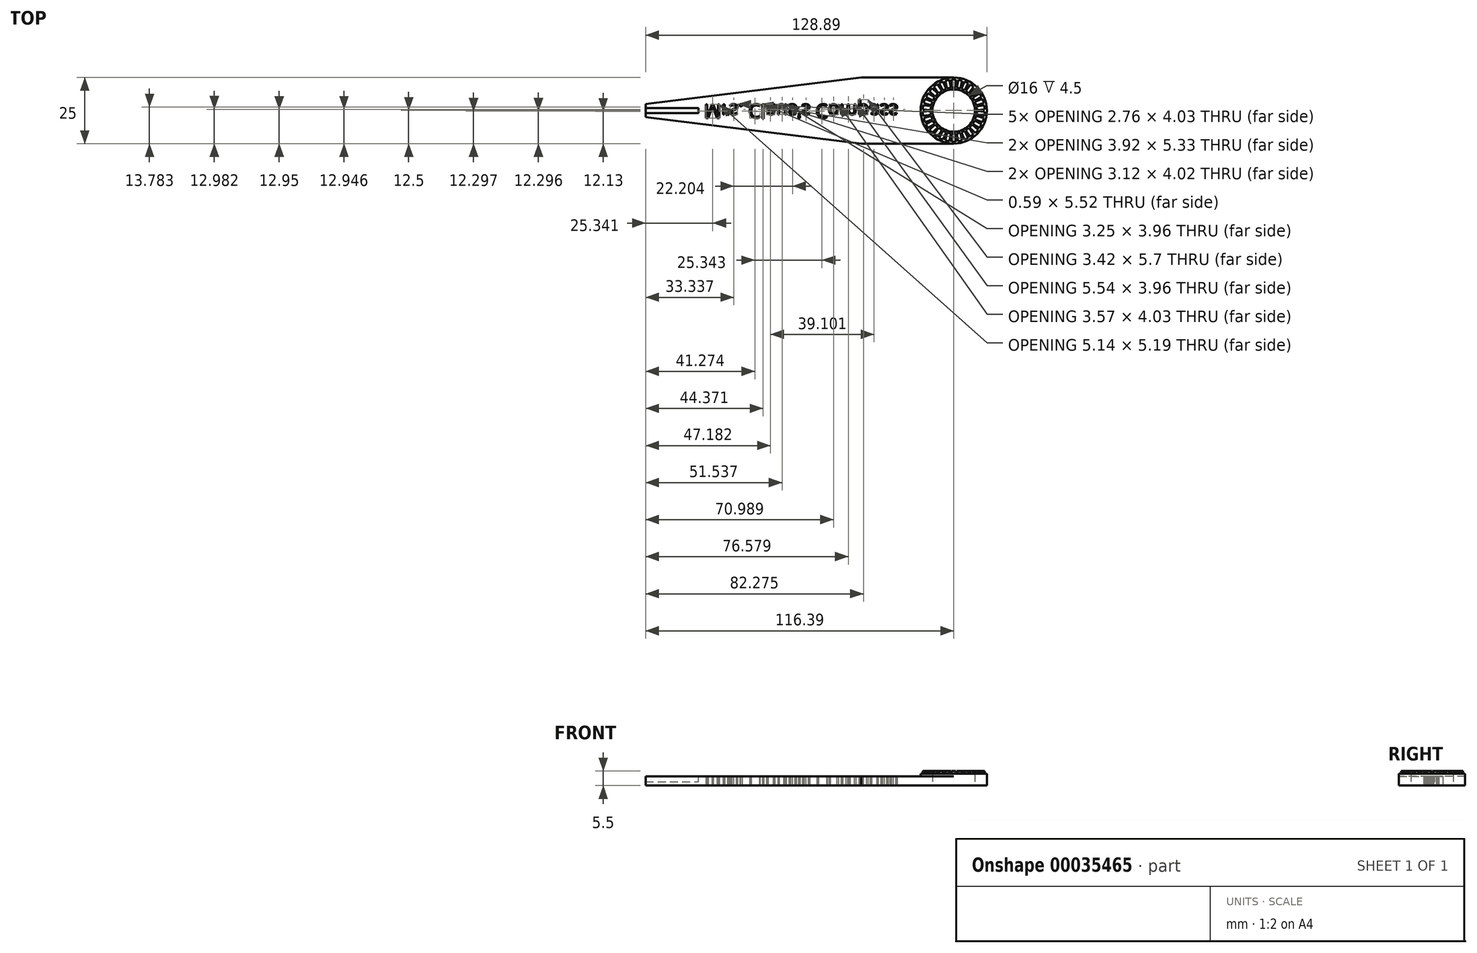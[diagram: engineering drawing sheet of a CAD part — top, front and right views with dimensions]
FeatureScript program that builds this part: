
annotation { "Feature Type Name" : "Feature", "Feature Type Description" : "" }
export const myFeature = defineFeature(function(context is Context, id is Id, definition is map)
    precondition{}
    {
        {
            var Q0;
            Q0=qCreatedBy(makeId("Top.planeOp"),FACE);
            var sketch = newSketch(context, id + "F0", { "sketchPlane" : qUnion([Q0])});
            skCircle(sketch, "E0", {"center": v(0, 0) * mm, "radius": 8 * mm});
            skCircle(sketch, "E1", {"center": v(0, 0) * mm, "radius": 12.5 * mm});
            skLineSegment(sketch, "E2", {"start": v(-35, 12.5) * mm, "end": v(0, 12.5) * mm});
            skLineSegment(sketch, "E3", {"start": v(-35, -12.5) * mm, "end": v(0, -12.5) * mm});
            skLineSegment(sketch, "E4", {"start": v(-35, 12.5) * mm, "end": v(-121.89, 12.5) * mm, "construction": true});
            skLineSegment(sketch, "E5", {"start": v(-35, 12.5) * mm, "end": v(-116.39, 2.5) * mm});
            skLineSegment(sketch, "E6", {"start": v(-35, -12.5) * mm, "end": v(-123.5, -12.5) * mm, "construction": true});
            skLineSegment(sketch, "E7", {"start": v(-35, -12.5) * mm, "end": v(-116.39, -2.5) * mm});
            skLineSegment(sketch, "E8", {"start": v(-116.39, 2.5) * mm, "end": v(-116.39, -2.5) * mm});
            skSolve(sketch);
        }
        {
            var Q0;
            Q0 = qSketchRegion(id + "F0", true);
            var Q1;
            Q1 = qSketchRegion(id + "F3", true);
            extrude(context, id + "F1", {"entities" : qUnion([Q0, Q1]), "depth" : 3.5 * mm});
        }
        {
            var Q0;
            Q0=makeQuery(id+"F1.opExtrude","CAP_FACE",FACE,{"disambiguationData":[OSD([sQuery(id+"F0.wireOp",EDGE,"E0"),sQuery(id+"F0.wireOp",EDGE,"E1"),sQuery(id+"F0.wireOp",EDGE,"E2"),sQuery(id+"F0.wireOp",EDGE,"E3"),sQuery(id+"F0.wireOp",EDGE,"E5"),sQuery(id+"F0.wireOp",EDGE,"E7"),sQuery(id+"F0.wireOp",EDGE,"E8")])],"isStart":false});
            var sketch = newSketch(context, id + "F2", { "sketchPlane" : qUnion([Q0])});
            skCircle(sketch, "E9", {"center": v(0, 0) * mm, "radius": 12.5 * mm});
            skCircle(sketch, "E10", {"center": v(0, 0) * mm, "radius": 8 * mm});
            skSolve(sketch);
        }
        {
            var Q0;
            {var subQ1=makeQuery(id+"F1.opExtrude","CAP_EDGE",EDGE,{"disambiguationData":[OSD([sQuery(id+"F0.wireOp",EDGE,"E2")])],"isStart":false});Q0=makeQuery(id+"F2.imprint","IMPRINT",FACE,{"disambiguationData":[TD([[makeQuery(id+"F2.imprint","IMPRINT",EDGE,{"derivedFrom":subQ1}),-1.0]])]});}
            var sketch = newSketch(context, id + "F3", { "sketchPlane" : qUnion([Q0])});
            skSolve(sketch);
        }
        {
            var Q0;
            {var subQ1=makeQuery(id+"F1.opExtrude","CAP_EDGE",EDGE,{"disambiguationData":[OSD([sQuery(id+"F0.wireOp",EDGE,"E2")])],"isStart":false});Q0=makeQuery(id+"F2.imprint","IMPRINT",FACE,{"disambiguationData":[TD([[makeQuery(id+"F2.imprint","IMPRINT",EDGE,{"derivedFrom":subQ1}),-1.0]])]});}
            var sketch = newSketch(context, id + "F4", { "sketchPlane" : qUnion([Q0])});
            skLineSegment(sketch, "E11.bottom", {"start": v(-116.39, 1) * mm, "end": v(-96.39, 1) * mm});
            skLineSegment(sketch, "E11.top", {"start": v(-116.39, -1) * mm, "end": v(-96.39, -1) * mm});
            skLineSegment(sketch, "E11.left", {"start": v(-116.39, 1) * mm, "end": v(-116.39, -1) * mm});
            skLineSegment(sketch, "E11.right", {"start": v(-96.39, 1) * mm, "end": v(-96.39, -1) * mm});
            skSolve(sketch);
        }
        {
            var Q0;
            Q0 = qSketchRegion(id + "F4", true);
            extrude(context, id + "F5", {"entities" : qUnion([Q0]), "operationType" : NewBodyOperationType.REMOVE, "oppositeDirection" : true, "depth" : 2 * mm});
        }
        {
            var Q0;
            Q0 = qSketchRegion(id + "F2", true);
            extrude(context, id + "F6", {"entities" : qUnion([Q0]), "operationType" : NewBodyOperationType.ADD, "depth" : 1 * mm});
        }
        {
            var Q0;
            Q0=makeQuery(id+"F6.opExtrude","CAP_FACE",FACE,{"disambiguationData":[OSD([sQuery(id+"F2.wireOp",EDGE,"E9"),sQuery(id+"F2.wireOp",EDGE,"E10")])],"isStart":false});
            var sketch = newSketch(context, id + "F7", { "sketchPlane" : qUnion([Q0])});
            skLineSegment(sketch, "E12.bottom", {"start": v(-0.74, 11.7) * mm, "end": v(0.76, 11.7) * mm});
            skLineSegment(sketch, "E12.top", {"start": v(-0.74, 8.7) * mm, "end": v(0.76, 8.7) * mm});
            skLineSegment(sketch, "E12.left", {"start": v(-0.74, 11.7) * mm, "end": v(-0.74, 8.7) * mm});
            skLineSegment(sketch, "E12.right", {"start": v(0.76, 11.7) * mm, "end": v(0.76, 8.7) * mm});
            skLineSegment(sketch, "E13.1.0", {"start": v(-3.16, 11.28) * mm, "end": v(-2.53, 8.35) * mm});
            skLineSegment(sketch, "E13.1.1", {"start": v(-2.53, 8.35) * mm, "end": v(-1.07, 8.66) * mm});
            skLineSegment(sketch, "E13.1.2", {"start": v(-1.7, 11.6) * mm, "end": v(-1.07, 8.66) * mm});
            skLineSegment(sketch, "E13.1.3", {"start": v(-3.16, 11.28) * mm, "end": v(-1.7, 11.6) * mm});
            skLineSegment(sketch, "E13.2.0", {"start": v(-5.44, 10.38) * mm, "end": v(-4.21, 7.64) * mm});
            skLineSegment(sketch, "E13.2.1", {"start": v(-4.21, 7.64) * mm, "end": v(-2.84, 8.25) * mm});
            skLineSegment(sketch, "E13.2.2", {"start": v(-4.06, 11) * mm, "end": v(-2.84, 8.25) * mm});
            skLineSegment(sketch, "E13.2.3", {"start": v(-5.44, 10.38) * mm, "end": v(-4.06, 11) * mm});
            skLineSegment(sketch, "E13.3.0", {"start": v(-7.47, 9.02) * mm, "end": v(-5.71, 6.6) * mm});
            skLineSegment(sketch, "E13.3.1", {"start": v(-5.71, 6.6) * mm, "end": v(-4.5, 7.48) * mm});
            skLineSegment(sketch, "E13.3.2", {"start": v(-6.26, 9.9) * mm, "end": v(-4.5, 7.48) * mm});
            skLineSegment(sketch, "E13.3.3", {"start": v(-7.47, 9.02) * mm, "end": v(-6.26, 9.9) * mm});
            skLineSegment(sketch, "E13.4.0", {"start": v(-9.19, 7.27) * mm, "end": v(-6.96, 5.27) * mm});
            skLineSegment(sketch, "E13.4.1", {"start": v(-6.96, 5.27) * mm, "end": v(-5.95, 6.38) * mm});
            skLineSegment(sketch, "E13.4.2", {"start": v(-8.18, 8.39) * mm, "end": v(-5.95, 6.38) * mm});
            skLineSegment(sketch, "E13.4.3", {"start": v(-9.19, 7.27) * mm, "end": v(-8.18, 8.39) * mm});
            skLineSegment(sketch, "E13.5.0", {"start": v(-10.5, 5.2) * mm, "end": v(-7.9, 3.7) * mm});
            skLineSegment(sketch, "E13.5.1", {"start": v(-7.9, 3.7) * mm, "end": v(-7.15, 5) * mm});
            skLineSegment(sketch, "E13.5.2", {"start": v(-9.75, 6.5) * mm, "end": v(-7.15, 5) * mm});
            skLineSegment(sketch, "E13.5.3", {"start": v(-10.5, 5.2) * mm, "end": v(-9.75, 6.5) * mm});
            skLineSegment(sketch, "E13.6.0", {"start": v(-11.35, 2.9) * mm, "end": v(-8.5, 1.98) * mm});
            skLineSegment(sketch, "E13.6.1", {"start": v(-8.5, 1.98) * mm, "end": v(-8.03, 3.4) * mm});
            skLineSegment(sketch, "E13.6.2", {"start": v(-10.89, 4.33) * mm, "end": v(-8.03, 3.4) * mm});
            skLineSegment(sketch, "E13.6.3", {"start": v(-11.35, 2.9) * mm, "end": v(-10.89, 4.33) * mm});
            skLineSegment(sketch, "E13.7.0", {"start": v(-11.7, 0.48) * mm, "end": v(-8.72, 0.17) * mm});
            skLineSegment(sketch, "E13.7.1", {"start": v(-8.72, 0.17) * mm, "end": v(-8.57, 1.66) * mm});
            skLineSegment(sketch, "E13.7.2", {"start": v(-11.55, 1.98) * mm, "end": v(-8.57, 1.66) * mm});
            skLineSegment(sketch, "E13.7.3", {"start": v(-11.7, 0.48) * mm, "end": v(-11.55, 1.98) * mm});
            skLineSegment(sketch, "E13.8.0", {"start": v(-11.55, -1.96) * mm, "end": v(-8.57, -1.65) * mm});
            skLineSegment(sketch, "E13.8.1", {"start": v(-8.57, -1.65) * mm, "end": v(-8.73, -0.16) * mm});
            skLineSegment(sketch, "E13.8.2", {"start": v(-11.7, -0.47) * mm, "end": v(-8.73, -0.16) * mm});
            skLineSegment(sketch, "E13.8.3", {"start": v(-11.55, -1.96) * mm, "end": v(-11.7, -0.47) * mm});
            skLineSegment(sketch, "E13.9.0", {"start": v(-10.9, -4.32) * mm, "end": v(-8.04, -3.4) * mm});
            skLineSegment(sketch, "E13.9.1", {"start": v(-8.04, -3.4) * mm, "end": v(-8.5, -1.97) * mm});
            skLineSegment(sketch, "E13.9.2", {"start": v(-11.36, -2.9) * mm, "end": v(-8.5, -1.97) * mm});
            skLineSegment(sketch, "E13.9.3", {"start": v(-10.9, -4.32) * mm, "end": v(-11.36, -2.9) * mm});
            skLineSegment(sketch, "E13.10.0", {"start": v(-9.76, -6.5) * mm, "end": v(-7.16, -5) * mm});
            skLineSegment(sketch, "E13.10.1", {"start": v(-7.16, -5) * mm, "end": v(-7.9, -3.7) * mm});
            skLineSegment(sketch, "E13.10.2", {"start": v(-10.5, -5.2) * mm, "end": v(-7.9, -3.7) * mm});
            skLineSegment(sketch, "E13.10.3", {"start": v(-9.76, -6.5) * mm, "end": v(-10.5, -5.2) * mm});
            skLineSegment(sketch, "E13.11.0", {"start": v(-8.2, -8.38) * mm, "end": v(-5.96, -6.37) * mm});
            skLineSegment(sketch, "E13.11.1", {"start": v(-5.96, -6.37) * mm, "end": v(-6.97, -5.25) * mm});
            skLineSegment(sketch, "E13.11.2", {"start": v(-9.2, -7.26) * mm, "end": v(-6.97, -5.25) * mm});
            skLineSegment(sketch, "E13.11.3", {"start": v(-8.2, -8.38) * mm, "end": v(-9.2, -7.26) * mm});
            skLineSegment(sketch, "E13.12.0", {"start": v(-6.27, -9.9) * mm, "end": v(-4.5, -7.47) * mm});
            skLineSegment(sketch, "E13.12.1", {"start": v(-4.5, -7.47) * mm, "end": v(-5.72, -6.59) * mm});
            skLineSegment(sketch, "E13.12.2", {"start": v(-7.49, -9.02) * mm, "end": v(-5.72, -6.59) * mm});
            skLineSegment(sketch, "E13.12.3", {"start": v(-6.27, -9.9) * mm, "end": v(-7.49, -9.02) * mm});
            skLineSegment(sketch, "E13.13.0", {"start": v(-4.08, -10.99) * mm, "end": v(-2.86, -8.24) * mm});
            skLineSegment(sketch, "E13.13.1", {"start": v(-2.86, -8.24) * mm, "end": v(-4.23, -7.63) * mm});
            skLineSegment(sketch, "E13.13.2", {"start": v(-5.45, -10.38) * mm, "end": v(-4.23, -7.63) * mm});
            skLineSegment(sketch, "E13.13.3", {"start": v(-4.08, -10.99) * mm, "end": v(-5.45, -10.38) * mm});
            skLineSegment(sketch, "E13.14.0", {"start": v(-1.7, -11.6) * mm, "end": v(-1.08, -8.66) * mm});
            skLineSegment(sketch, "E13.14.1", {"start": v(-1.08, -8.66) * mm, "end": v(-2.55, -8.35) * mm});
            skLineSegment(sketch, "E13.14.2", {"start": v(-3.17, -11.28) * mm, "end": v(-2.55, -8.35) * mm});
            skLineSegment(sketch, "E13.14.3", {"start": v(-1.7, -11.6) * mm, "end": v(-3.17, -11.28) * mm});
            skLineSegment(sketch, "E13.15.0", {"start": v(0.74, -11.7) * mm, "end": v(0.74, -8.7) * mm});
            skLineSegment(sketch, "E13.15.1", {"start": v(0.74, -8.7) * mm, "end": v(-0.76, -8.7) * mm});
            skLineSegment(sketch, "E13.15.2", {"start": v(-0.76, -11.7) * mm, "end": v(-0.76, -8.7) * mm});
            skLineSegment(sketch, "E13.15.3", {"start": v(0.74, -11.7) * mm, "end": v(-0.76, -11.7) * mm});
            skLineSegment(sketch, "E13.16.0", {"start": v(3.16, -11.28) * mm, "end": v(2.53, -8.35) * mm});
            skLineSegment(sketch, "E13.16.1", {"start": v(2.53, -8.35) * mm, "end": v(1.07, -8.66) * mm});
            skLineSegment(sketch, "E13.16.2", {"start": v(1.7, -11.6) * mm, "end": v(1.07, -8.66) * mm});
            skLineSegment(sketch, "E13.16.3", {"start": v(3.16, -11.28) * mm, "end": v(1.7, -11.6) * mm});
            skLineSegment(sketch, "E13.17.0", {"start": v(5.44, -10.38) * mm, "end": v(4.21, -7.64) * mm});
            skLineSegment(sketch, "E13.17.1", {"start": v(4.21, -7.64) * mm, "end": v(2.84, -8.25) * mm});
            skLineSegment(sketch, "E13.17.2", {"start": v(4.06, -11) * mm, "end": v(2.84, -8.25) * mm});
            skLineSegment(sketch, "E13.17.3", {"start": v(5.44, -10.38) * mm, "end": v(4.06, -11) * mm});
            skLineSegment(sketch, "E13.18.0", {"start": v(7.47, -9.02) * mm, "end": v(5.71, -6.6) * mm});
            skLineSegment(sketch, "E13.18.1", {"start": v(5.71, -6.6) * mm, "end": v(4.5, -7.48) * mm});
            skLineSegment(sketch, "E13.18.2", {"start": v(6.26, -9.9) * mm, "end": v(4.5, -7.48) * mm});
            skLineSegment(sketch, "E13.18.3", {"start": v(7.47, -9.02) * mm, "end": v(6.26, -9.9) * mm});
            skLineSegment(sketch, "E13.19.0", {"start": v(9.19, -7.27) * mm, "end": v(6.96, -5.27) * mm});
            skLineSegment(sketch, "E13.19.1", {"start": v(6.96, -5.27) * mm, "end": v(5.95, -6.38) * mm});
            skLineSegment(sketch, "E13.19.2", {"start": v(8.18, -8.39) * mm, "end": v(5.95, -6.38) * mm});
            skLineSegment(sketch, "E13.19.3", {"start": v(9.19, -7.27) * mm, "end": v(8.18, -8.39) * mm});
            skLineSegment(sketch, "E13.20.0", {"start": v(10.5, -5.2) * mm, "end": v(7.9, -3.7) * mm});
            skLineSegment(sketch, "E13.20.1", {"start": v(7.9, -3.7) * mm, "end": v(7.15, -5) * mm});
            skLineSegment(sketch, "E13.20.2", {"start": v(9.75, -6.5) * mm, "end": v(7.15, -5) * mm});
            skLineSegment(sketch, "E13.20.3", {"start": v(10.5, -5.2) * mm, "end": v(9.75, -6.5) * mm});
            skLineSegment(sketch, "E13.21.0", {"start": v(11.35, -2.9) * mm, "end": v(8.5, -1.98) * mm});
            skLineSegment(sketch, "E13.21.1", {"start": v(8.5, -1.98) * mm, "end": v(8.03, -3.4) * mm});
            skLineSegment(sketch, "E13.21.2", {"start": v(10.89, -4.33) * mm, "end": v(8.03, -3.4) * mm});
            skLineSegment(sketch, "E13.21.3", {"start": v(11.35, -2.9) * mm, "end": v(10.89, -4.33) * mm});
            skLineSegment(sketch, "E13.22.0", {"start": v(11.7, -0.48) * mm, "end": v(8.72, -0.17) * mm});
            skLineSegment(sketch, "E13.22.1", {"start": v(8.72, -0.17) * mm, "end": v(8.57, -1.66) * mm});
            skLineSegment(sketch, "E13.22.2", {"start": v(11.55, -1.98) * mm, "end": v(8.57, -1.66) * mm});
            skLineSegment(sketch, "E13.22.3", {"start": v(11.7, -0.48) * mm, "end": v(11.55, -1.98) * mm});
            skLineSegment(sketch, "E13.23.0", {"start": v(11.55, 1.96) * mm, "end": v(8.57, 1.65) * mm});
            skLineSegment(sketch, "E13.23.1", {"start": v(8.57, 1.65) * mm, "end": v(8.73, 0.16) * mm});
            skLineSegment(sketch, "E13.23.2", {"start": v(11.7, 0.47) * mm, "end": v(8.73, 0.16) * mm});
            skLineSegment(sketch, "E13.23.3", {"start": v(11.55, 1.96) * mm, "end": v(11.7, 0.47) * mm});
            skLineSegment(sketch, "E13.24.0", {"start": v(10.9, 4.32) * mm, "end": v(8.04, 3.4) * mm});
            skLineSegment(sketch, "E13.24.1", {"start": v(8.04, 3.4) * mm, "end": v(8.5, 1.97) * mm});
            skLineSegment(sketch, "E13.24.2", {"start": v(11.36, 2.9) * mm, "end": v(8.5, 1.97) * mm});
            skLineSegment(sketch, "E13.24.3", {"start": v(10.9, 4.32) * mm, "end": v(11.36, 2.9) * mm});
            skLineSegment(sketch, "E13.25.0", {"start": v(9.76, 6.5) * mm, "end": v(7.16, 5) * mm});
            skLineSegment(sketch, "E13.25.1", {"start": v(7.16, 5) * mm, "end": v(7.9, 3.7) * mm});
            skLineSegment(sketch, "E13.25.2", {"start": v(10.5, 5.2) * mm, "end": v(7.9, 3.7) * mm});
            skLineSegment(sketch, "E13.25.3", {"start": v(9.76, 6.5) * mm, "end": v(10.5, 5.2) * mm});
            skLineSegment(sketch, "E13.26.0", {"start": v(8.2, 8.38) * mm, "end": v(5.96, 6.37) * mm});
            skLineSegment(sketch, "E13.26.1", {"start": v(5.96, 6.37) * mm, "end": v(6.97, 5.25) * mm});
            skLineSegment(sketch, "E13.26.2", {"start": v(9.2, 7.26) * mm, "end": v(6.97, 5.25) * mm});
            skLineSegment(sketch, "E13.26.3", {"start": v(8.2, 8.38) * mm, "end": v(9.2, 7.26) * mm});
            skLineSegment(sketch, "E13.27.0", {"start": v(6.27, 9.9) * mm, "end": v(4.5, 7.47) * mm});
            skLineSegment(sketch, "E13.27.1", {"start": v(4.5, 7.47) * mm, "end": v(5.72, 6.59) * mm});
            skLineSegment(sketch, "E13.27.2", {"start": v(7.49, 9.02) * mm, "end": v(5.72, 6.59) * mm});
            skLineSegment(sketch, "E13.27.3", {"start": v(6.27, 9.9) * mm, "end": v(7.49, 9.02) * mm});
            skLineSegment(sketch, "E13.28.0", {"start": v(4.08, 10.99) * mm, "end": v(2.86, 8.24) * mm});
            skLineSegment(sketch, "E13.28.1", {"start": v(2.86, 8.24) * mm, "end": v(4.23, 7.63) * mm});
            skLineSegment(sketch, "E13.28.2", {"start": v(5.45, 10.38) * mm, "end": v(4.23, 7.63) * mm});
            skLineSegment(sketch, "E13.28.3", {"start": v(4.08, 10.99) * mm, "end": v(5.45, 10.38) * mm});
            skLineSegment(sketch, "E13.29.0", {"start": v(1.7, 11.6) * mm, "end": v(1.08, 8.66) * mm});
            skLineSegment(sketch, "E13.29.1", {"start": v(1.08, 8.66) * mm, "end": v(2.55, 8.35) * mm});
            skLineSegment(sketch, "E13.29.2", {"start": v(3.17, 11.28) * mm, "end": v(2.55, 8.35) * mm});
            skLineSegment(sketch, "E13.29.3", {"start": v(1.7, 11.6) * mm, "end": v(3.17, 11.28) * mm});
            skPoint(sketch, "E13.center", {"position": v(0, 0) * mm});
            skSolve(sketch);
        }
        {
            var Q0;
            Q0 = qSketchRegion(id + "F7", true);
            extrude(context, id + "F8", {"entities" : qUnion([Q0]), "operationType" : NewBodyOperationType.ADD, "depth" : 1 * mm});
        }
        {
            var Q0;
            Q0=makeQuery(id+"F1.opExtrude","CAP_FACE",FACE,{"disambiguationData":[OSD([sQuery(id+"F0.wireOp",EDGE,"E0"),sQuery(id+"F0.wireOp",EDGE,"E1"),sQuery(id+"F0.wireOp",EDGE,"E2"),sQuery(id+"F0.wireOp",EDGE,"E3"),sQuery(id+"F0.wireOp",EDGE,"E5"),sQuery(id+"F0.wireOp",EDGE,"E7"),sQuery(id+"F0.wireOp",EDGE,"E8")])],"isStart":true});
            var sketch = newSketch(context, id + "F9", { "sketchPlane" : qUnion([Q0])});
            skText(sketch, "E14", { "text": "Mrs. Claus\'s Compass", "fontName": "OpenSans-Regular.ttf"});
            const initialGuessF9  = {"E14": [-0.09433, -0.00239, 1, 0, 0.00523]};
            skSetInitialGuess(sketch, initialGuessF9);
            skSolve(sketch);
        }
        {
            var Q0;
            Q0 = qSketchRegion(id + "F9", true);
            extrude(context, id + "F10", {"entities" : qUnion([Q0]), "operationType" : NewBodyOperationType.REMOVE, "endBound" : BoundingType.THROUGH_ALL, "oppositeDirection" : true, "depth" : .3 * mm});
        }
    });
